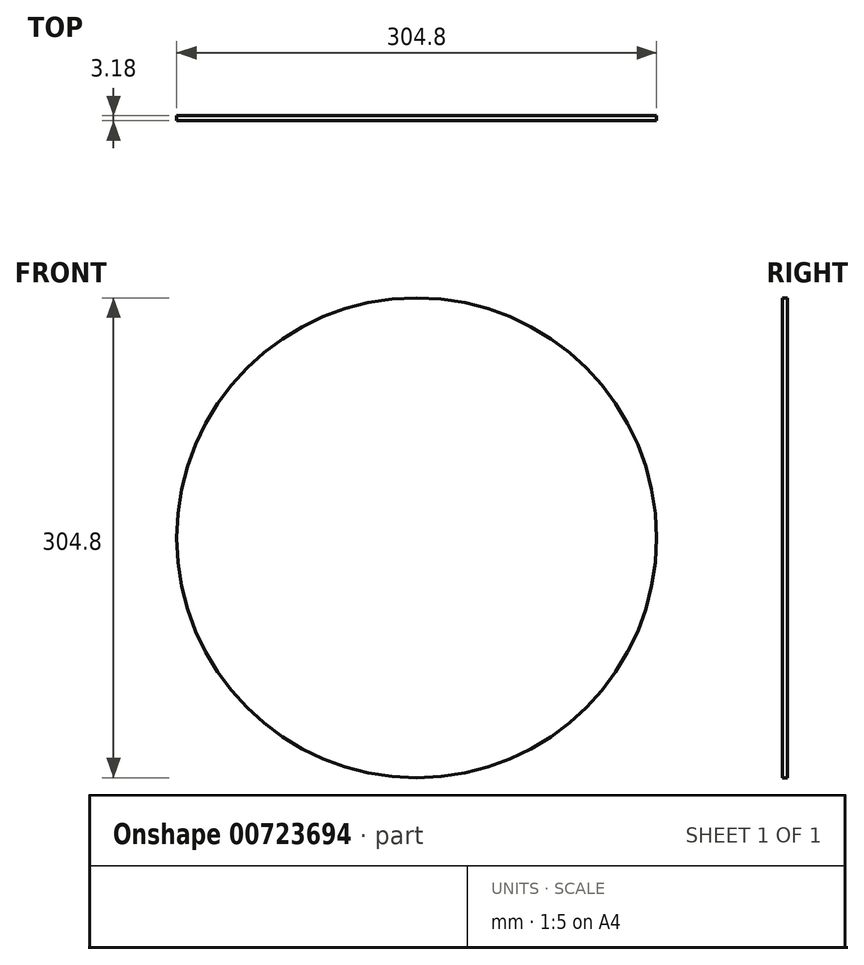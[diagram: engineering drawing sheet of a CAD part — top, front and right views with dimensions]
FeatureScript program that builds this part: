
annotation { "Feature Type Name" : "Feature", "Feature Type Description" : "" }
export const myFeature = defineFeature(function(context is Context, id is Id, definition is map)
    precondition{}
    {
        {
            var Q0;
            Q0=qCreatedBy(makeId("Front.planeOp"),FACE);
            var sketch = newSketch(context, id + "F0", { "sketchPlane" : qUnion([Q0])});
            skCircle(sketch, "E0", {"center": v(0, 0) * mm, "radius": 152.4 * mm});
            skSolve(sketch);
        }
        {
            var Q0;
            Q0 = qSketchRegion(id + "F0", true);
            extrude(context, id + "F1", {"entities" : qUnion([Q0]), "depth" : 3.17 * mm, "offsetDistance" : 25.4 * mm});
        }
    });
